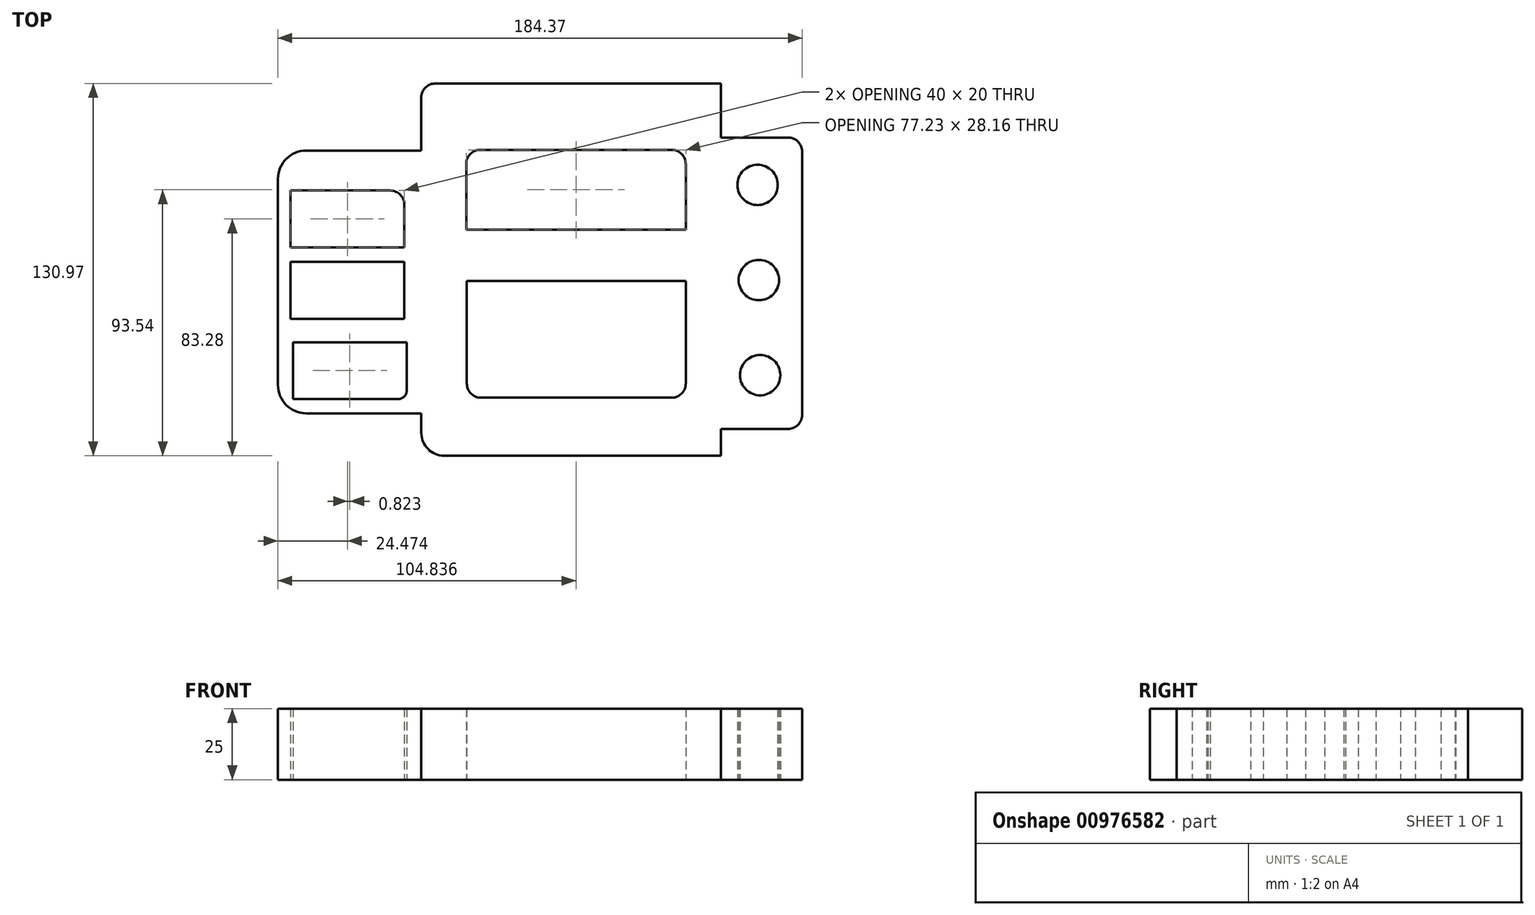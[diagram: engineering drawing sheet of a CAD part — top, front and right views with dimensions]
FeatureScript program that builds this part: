
annotation { "Feature Type Name" : "Feature", "Feature Type Description" : "" }
export const myFeature = defineFeature(function(context is Context, id is Id, definition is map)
    precondition{}
    {
        {
            var Q0;
            Q0=qCreatedBy(makeId("Top.planeOp"),FACE);
            var sketch = newSketch(context, id + "F0", { "sketchPlane" : qUnion([Q0])});
            skLineSegment(sketch, "E0.left", {"start": v(-143.45, 35.85) * mm, "end": v(-143.45, -36.6) * mm});
            skLineSegment(sketch, "E1.bottom", {"start": v(-88.02, 69.48) * mm, "end": v(12.3, 69.48) * mm});
            skLineSegment(sketch, "E1.top", {"start": v(-85.02, -61.5) * mm, "end": v(12.3, -61.5) * mm});
            skLineSegment(sketch, "E2.bottom", {"start": v(12.3, 50.45) * mm, "end": v(35.92, 50.45) * mm});
            skLineSegment(sketch, "E2.top", {"start": v(12.3, -52.1) * mm, "end": v(35.92, -52.1) * mm});
            skLineSegment(sketch, "E2.right", {"start": v(40.92, 45.45) * mm, "end": v(40.92, -47.1) * mm});
            skLineSegment(sketch, "E3.bottom", {"start": v(-72.23, 46.13) * mm, "end": v(-5, 46.13) * mm});
            skLineSegment(sketch, "E3.top", {"start": v(-77.23, 17.97) * mm, "end": v(0, 17.97) * mm});
            skLineSegment(sketch, "E3.left", {"start": v(-77.23, 41.13) * mm, "end": v(-77.23, 17.97) * mm});
            skLineSegment(sketch, "E3.right", {"start": v(0, 41.13) * mm, "end": v(0, 17.97) * mm});
            skLineSegment(sketch, "E4.bottom", {"start": v(-77, 0) * mm, "end": v(0, 0) * mm});
            skLineSegment(sketch, "E4.top", {"start": v(-72, -41.1) * mm, "end": v(-5, -41.1) * mm});
            skLineSegment(sketch, "E4.left", {"start": v(-77, 0) * mm, "end": v(-77, -36.1) * mm});
            skLineSegment(sketch, "E4.right", {"start": v(0, 0) * mm, "end": v(0, -36.1) * mm});
            skLineSegment(sketch, "E5.bottom", {"start": v(-138.98, 31.79) * mm, "end": v(-103.98, 31.79) * mm});
            skLineSegment(sketch, "E5.top", {"start": v(-138.98, 11.79) * mm, "end": v(-98.98, 11.79) * mm});
            skLineSegment(sketch, "E5.left", {"start": v(-138.98, 31.79) * mm, "end": v(-138.98, 11.79) * mm});
            skLineSegment(sketch, "E5.right", {"start": v(-98.98, 26.79) * mm, "end": v(-98.98, 11.79) * mm});
            skLineSegment(sketch, "E6.bottom", {"start": v(-138.98, 6.7) * mm, "end": v(-98.98, 6.7) * mm});
            skLineSegment(sketch, "E6.top", {"start": v(-138.98, -13.3) * mm, "end": v(-98.98, -13.3) * mm});
            skLineSegment(sketch, "E6.left", {"start": v(-138.98, 6.7) * mm, "end": v(-138.98, -13.3) * mm});
            skLineSegment(sketch, "E6.right", {"start": v(-98.98, 6.7) * mm, "end": v(-98.98, -13.3) * mm});
            skLineSegment(sketch, "E7.bottom", {"start": v(-138.15, -21.57) * mm, "end": v(-98.15, -21.57) * mm});
            skLineSegment(sketch, "E7.top", {"start": v(-138.15, -41.57) * mm, "end": v(-101.15, -41.57) * mm});
            skLineSegment(sketch, "E7.left", {"start": v(-138.15, -21.57) * mm, "end": v(-138.15, -41.57) * mm});
            skLineSegment(sketch, "E7.right", {"start": v(-98.15, -21.57) * mm, "end": v(-98.15, -38.57) * mm});
            skPoint(sketch, "E8.visualSharp", {"position": v(-93.02, 69.48) * mm});
            skArc(sketch, "E8.filletArc", {"start": v(-88.02, 69.48) * mm, "mid": v(-91.56, 68.01) * mm, "end": v(-93.02, 64.48) * mm});
            skPoint(sketch, "E9.visualSharp", {"position": v(-93.02, -61.5) * mm});
            skArc(sketch, "E9.filletArc", {"start": v(-93.02, -53.5) * mm, "mid": v(-90.68, -59.15) * mm, "end": v(-85.02, -61.5) * mm});
            skPoint(sketch, "E10.visualSharp", {"position": v(-98.98, 31.79) * mm});
            skArc(sketch, "E10.filletArc", {"start": v(-98.98, 26.79) * mm, "mid": v(-100.44, 30.33) * mm, "end": v(-103.98, 31.79) * mm});
            skPoint(sketch, "E11.visualSharp", {"position": v(-98.15, -41.57) * mm});
            skArc(sketch, "E11.filletArc", {"start": v(-101.15, -41.57) * mm, "mid": v(-99.03, -40.7) * mm, "end": v(-98.15, -38.57) * mm});
            skPoint(sketch, "E12.visualSharp", {"position": v(-77.23, 46.13) * mm});
            skArc(sketch, "E12.filletArc", {"start": v(-72.23, 46.13) * mm, "mid": v(-75.76, 44.66) * mm, "end": v(-77.23, 41.13) * mm});
            skPoint(sketch, "E13.visualSharp", {"position": v(0, 46.13) * mm});
            skArc(sketch, "E13.filletArc", {"start": v(0, 41.13) * mm, "mid": v(-1.46, 44.66) * mm, "end": v(-5, 46.13) * mm});
            skPoint(sketch, "E14.visualSharp", {"position": v(-77, -41.1) * mm});
            skArc(sketch, "E14.filletArc", {"start": v(-77, -36.1) * mm, "mid": v(-75.53, -39.63) * mm, "end": v(-72, -41.1) * mm});
            skPoint(sketch, "E15.visualSharp", {"position": v(0, -41.1) * mm});
            skArc(sketch, "E15.filletArc", {"start": v(-5, -41.1) * mm, "mid": v(-1.46, -39.63) * mm, "end": v(0, -36.1) * mm});
            skPoint(sketch, "E16.visualSharp", {"position": v(40.92, 50.45) * mm});
            skArc(sketch, "E16.filletArc", {"start": v(40.92, 45.45) * mm, "mid": v(39.46, 48.99) * mm, "end": v(35.92, 50.45) * mm});
            skPoint(sketch, "E17.visualSharp", {"position": v(40.92, -52.1) * mm});
            skArc(sketch, "E17.filletArc", {"start": v(35.92, -52.1) * mm, "mid": v(39.46, -50.64) * mm, "end": v(40.92, -47.1) * mm});
            skCircle(sketch, "E18", {"center": v(25.24, 33.77) * mm, "radius": 7.1 * mm});
            skCircle(sketch, "E19.1.0.0", {"center": v(25.7, 0.3) * mm, "radius": 7.1 * mm});
            skCircle(sketch, "E19.2.0.0", {"center": v(26.16, -33.17) * mm, "radius": 7.1 * mm});
            skLineSegment(sketch, "E19.direction1", {"start": v(25.24, 33.77) * mm, "end": v(25.7, 0.3) * mm, "construction": true});
            skPoint(sketch, "E20.visualSharp", {"position": v(-143.45, 45.85) * mm});
            skArc(sketch, "E20.filletArc", {"start": v(-133.45, 45.85) * mm, "mid": v(-140.52, 42.92) * mm, "end": v(-143.45, 35.85) * mm});
            skPoint(sketch, "E21.visualSharp", {"position": v(-143.45, -46.6) * mm});
            skArc(sketch, "E21.filletArc", {"start": v(-143.45, -36.6) * mm, "mid": v(-140.52, -43.67) * mm, "end": v(-133.45, -46.6) * mm});
            skLineSegment(sketch, "E22", {"start": v(12.3, 69.48) * mm, "end": v(12.3, 50.45) * mm});
            skLineSegment(sketch, "E23", {"start": v(12.3, -52.1) * mm, "end": v(12.3, -61.5) * mm});
            skLineSegment(sketch, "E24", {"start": v(-93.02, 64.48) * mm, "end": v(-93.02, 45.85) * mm});
            skLineSegment(sketch, "E25", {"start": v(-93.02, -46.6) * mm, "end": v(-93.02, -53.5) * mm});
            skLineSegment(sketch, "E26", {"start": v(-133.45, 45.85) * mm, "end": v(-93.02, 45.85) * mm});
            skLineSegment(sketch, "E27", {"start": v(-133.45, -46.6) * mm, "end": v(-93.02, -46.6) * mm});
            skSolve(sketch);
        }
        {
            var Q0;
            Q0 = qSketchRegion(id + "F0", true);
            extrude(context, id + "F1", {"entities" : qUnion([Q0]), "depth" : 25 * mm, "offsetDistance" : 25 * mm});
        }
        {
            var Q0;
            Q0=makeQuery(id+"F1.opExtrude","SWEPT_EDGE",EDGE,{"disambiguationData":[OSD([sQuery(id+"F0.wireOp",EDGE,"E1.top"),sQuery(id+"F0.wireOp",EDGE,"E23")])]});
            var Q1;
            Q1=makeQuery(id+"F1.opExtrude","SWEPT_EDGE",EDGE,{"disambiguationData":[OSD([sQuery(id+"F0.wireOp",EDGE,"E1.top"),sQuery(id+"F0.wireOp",EDGE,"E9.filletArc")])]});
            fillet(context, id + "F2", {"entities" : qUnion([Q0, Q1]), "radius" : 5 * mm, "tangentPropagation" : true, "allowEdgeOverflow" : false});
        }
        {
            var Q0;
            Q0 = qSketchRegion(id + "F0", true);
            extrude(context, id + "F3", {"entities" : qUnion([Q0]), "operationType" : NewBodyOperationType.ADD, "depth" : 25 * mm, "offsetDistance" : 25 * mm});
        }
    });
